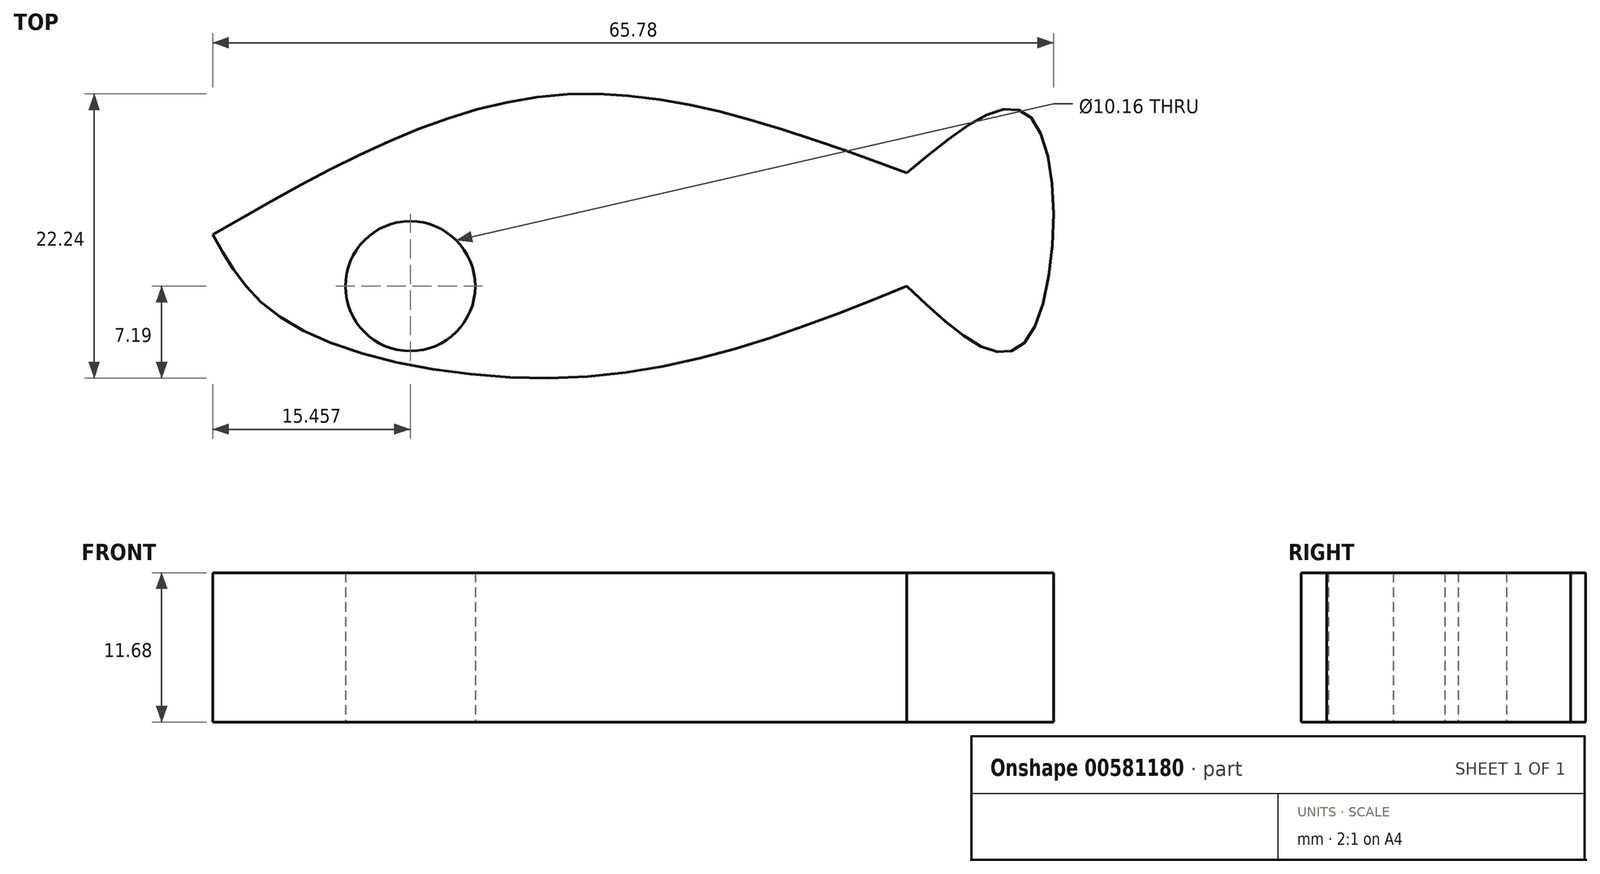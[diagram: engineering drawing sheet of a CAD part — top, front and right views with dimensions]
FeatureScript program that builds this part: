
annotation { "Feature Type Name" : "Feature", "Feature Type Description" : "" }
export const myFeature = defineFeature(function(context is Context, id is Id, definition is map)
    precondition{}
    {
        {
            var Q0;
            Q0=qCreatedBy(makeId("Top.planeOp"),FACE);
            var sketch = newSketch(context, id + "F0", { "sketchPlane" : qUnion([Q0])});
            skFitSpline(sketch, "E0", {"points": [v(-36.12, 4.03) * mm, v(-9.38, 14.94) * mm, v(18.18, 8.86) * mm], "startDerivative": vector(52.6, 30.23) * mm, "endDerivative": vector(56, -20.68) * mm});
            skFitSpline(sketch, "E1", {"points": [v(-36.12, 4.03) * mm, v(-30.38, -2.73) * mm, v(-6.97, -7.08) * mm, v(18.18, 0) * mm], "startDerivative": vector(17.43, -31.63) * mm, "endDerivative": vector(61.05, 24.6) * mm});
            skFitSpline(sketch, "E2", {"points": [v(18.18, 8.86) * mm, v(27.95, 13.14) * mm, v(27.26, -4.55) * mm, v(18.18, 0) * mm], "startDerivative": vector(37.94, 32) * mm, "endDerivative": vector(-34.85, 33.17) * mm});
            skSolve(sketch);
        }
        {
            var Q0;
            Q0 = qSketchRegion(id + "F0", true);
            extrude(context, id + "F1", {"entities" : qUnion([Q0]), "depth" : 11.68 * mm, "offsetDistance" : 25.4 * mm});
        }
        {
            var Q0;
            Q0=qCreatedBy(makeId("Top.planeOp"),FACE);
            var sketch = newSketch(context, id + "F2", { "sketchPlane" : qUnion([Q0])});
            skCircle(sketch, "E3", {"center": v(-20.66, 0) * mm, "radius": 4.4 * mm});
            skSolve(sketch);
        }
        {
            var Q0;
            Q0=sQuery(id+"F2.wireOp",VERTEX,"E3.center");
            var Q1;
            Q1=makeQuery(id+"F1.opExtrude","SWEPT_BODY",BODY,{"disambiguationData":[OSD([sQuery(id+"F0.wireOp",EDGE,"E0"),sQuery(id+"F0.wireOp",EDGE,"E1"),sQuery(id+"F0.wireOp",EDGE,"E2")])]});
            hole(context, id + "F3", {"style" : HoleStyle.SIMPLE, "endStyle" : HoleEndStyle.THROUGH, "oppositeDirection" : true, "holeDiameter" : 10.16 * mm, "majorDiameter" : 6.35 * mm, "isTappedThrough" : true, "tappedDepth" : 12.7 * mm, "tapClearance" : 3, "locations" : qUnion([Q0]), "scope" : qUnion([Q1])});
        }
    });
